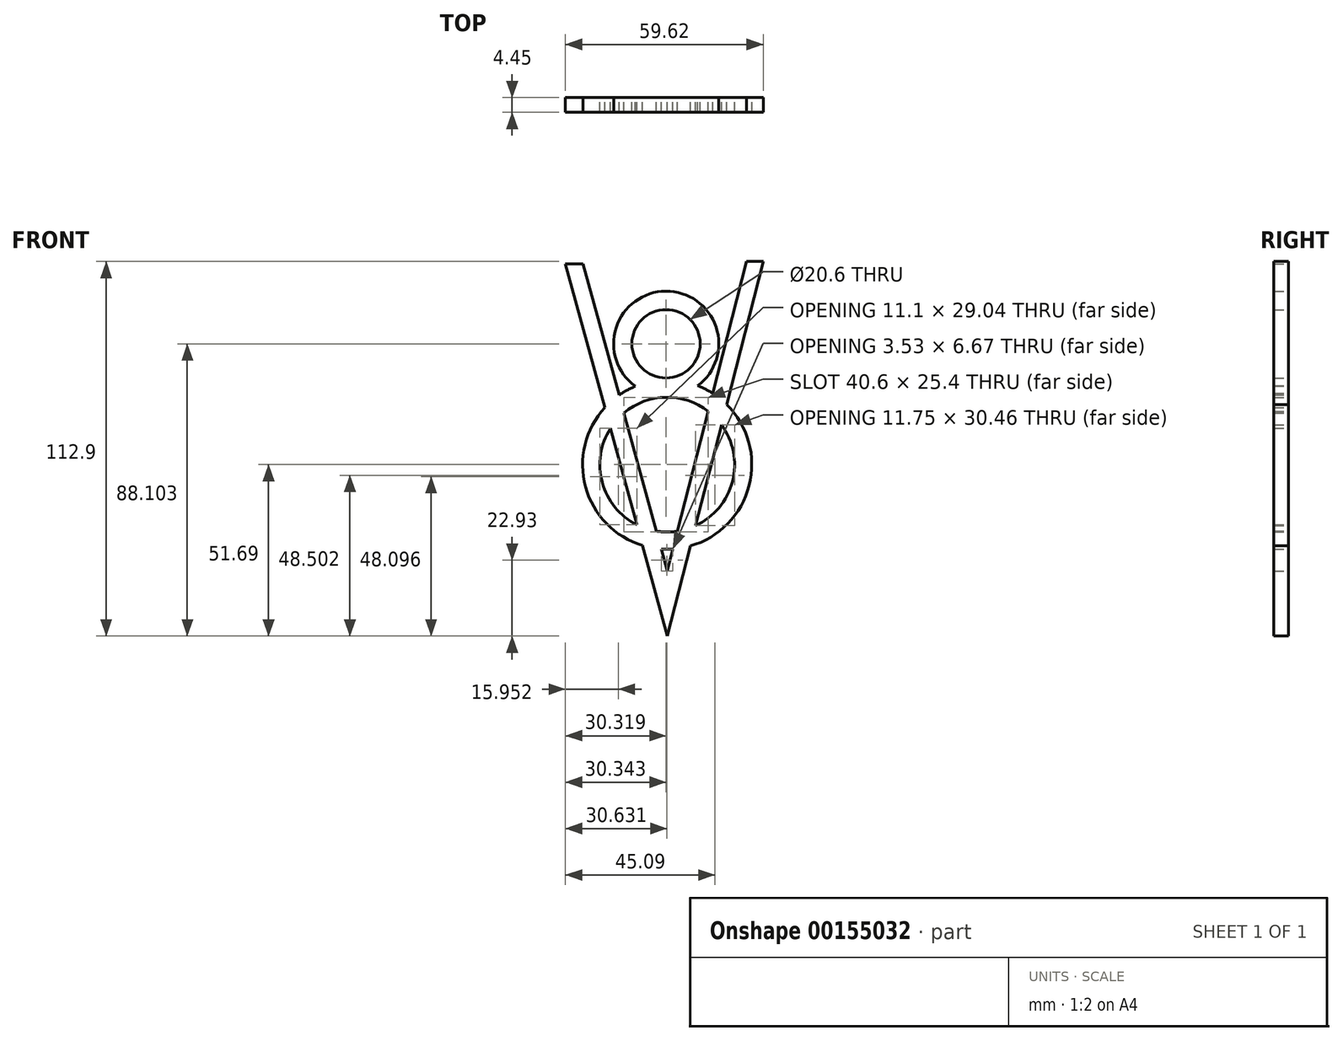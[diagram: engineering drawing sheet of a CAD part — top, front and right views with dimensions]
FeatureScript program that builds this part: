
annotation { "Feature Type Name" : "Feature", "Feature Type Description" : "" }
export const myFeature = defineFeature(function(context is Context, id is Id, definition is map)
    precondition{}
    {
        {
            var Q0;
            Q0=qCreatedBy(makeId("Front.planeOp"),FACE);
            var sketch = newSketch(context, id + "F0", { "sketchPlane" : qUnion([Q0])});
            skLineSegment(sketch, "E0", {"start": v(0, -70.05) * mm, "end": v(-7.47, -42.73) * mm});
            skLineSegment(sketch, "E1", {"start": v(-30.7, 42.12) * mm, "end": v(-25.33, 42.12) * mm});
            skLineSegment(sketch, "E2", {"start": v(-25.33, 42.12) * mm, "end": v(-14.52, 2.6) * mm});
            skLineSegment(sketch, "E3", {"start": v(0, -50.45) * mm, "end": v(1.7, -43.8) * mm});
            skLineSegment(sketch, "E4", {"start": v(23.9, 42.85) * mm, "end": v(28.93, 42.85) * mm});
            skLineSegment(sketch, "E5", {"start": v(28.93, 42.85) * mm, "end": v(17.9, -0.22) * mm});
            skArc(sketch, "E6", {"start": v(-9.6, 5.26) * mm, "mid": v(-12.13, 4.07) * mm, "end": v(-14.52, 2.6) * mm});
            skPoint(sketch, "E6.first.point", {"position": v(-24.9, -12.84) * mm});
            skPoint(sketch, "E6.second.point", {"position": v(13.12, -40.2) * mm});
            skPoint(sketch, "E6.third.point", {"position": v(23.56, -8.67) * mm});
            skPoint(sketch, "E7.first.point", {"position": v(19.2, 21.93) * mm});
            skPoint(sketch, "E7.second.point", {"position": v(-11.63, 34.45) * mm});
            skPoint(sketch, "E7.third.point", {"position": v(-14.88, 4.54) * mm});
            skArc(sketch, "E8", {"start": v(9.18, 5.41) * mm, "mid": v(-0.44, 33.93) * mm, "end": v(-9.6, 5.26) * mm});
            skPoint(sketch, "E8.first.point", {"position": v(-13.59, 26.73) * mm});
            skPoint(sketch, "E8.second.point", {"position": v(14, 24.88) * mm});
            skPoint(sketch, "E8.third.point", {"position": v(11.45, 7.49) * mm});
            skCircle(sketch, "E9", {"center": v(-0.37, 18.05) * mm, "radius": 10.3 * mm});
            skPoint(sketch, "E9.first.point", {"position": v(3.34, 27.66) * mm});
            skPoint(sketch, "E9.second.point", {"position": v(8.2, 12.36) * mm});
            skPoint(sketch, "E9.third.point", {"position": v(-8.26, 11.43) * mm});
            skArc(sketch, "E10", {"start": v(-17.13, -7.43) * mm, "mid": v(-19.6, -23.72) * mm, "end": v(-9.19, -36.48) * mm});
            skPoint(sketch, "E10.first.point", {"position": v(-18.52, -10) * mm});
            skPoint(sketch, "E10.second.point", {"position": v(19.1, -11.55) * mm});
            skPoint(sketch, "E10.third.point", {"position": v(11.95, -34.76) * mm});
            skPoint(sketch, "E10.third.point.positionSnap0", {"position": v(11.95, -3.8) * mm});
            skLineSegment(sketch, "E11.trimOffspring", {"start": v(-13.05, -2.78) * mm, "end": v(-3.3, -38.4) * mm});
            skLineSegment(sketch, "E12.trimOffspring", {"start": v(-18.85, -1.17) * mm, "end": v(-30.7, 42.12) * mm});
            skArc(sketch, "E13.trimOffspring", {"start": v(-18.85, -1.17) * mm, "mid": v(-24.6, -25.09) * mm, "end": v(-7.47, -42.73) * mm});
            skArc(sketch, "E14.trimOffspring", {"start": v(12.35, -2.26) * mm, "mid": v(-0.44, 1.94) * mm, "end": v(-13.05, -2.78) * mm});
            skLineSegment(sketch, "E15.trimOffspring", {"start": v(13.73, 3.1) * mm, "end": v(23.9, 42.85) * mm});
            skLineSegment(sketch, "E16.trimOffspring", {"start": v(16.33, -6.32) * mm, "end": v(8.53, -36.78) * mm});
            skArc(sketch, "E17.trimOffspring", {"start": v(-3.3, -38.4) * mm, "mid": v(-0.1, -38.66) * mm, "end": v(3.08, -38.42) * mm});
            skArc(sketch, "E18.trimOffspring", {"start": v(-1.83, -43.78) * mm, "mid": v(-0.06, -43.85) * mm, "end": v(1.7, -43.8) * mm});
            skLineSegment(sketch, "E19.trimOffspring", {"start": v(-9.19, -36.48) * mm, "end": v(-17.13, -7.43) * mm});
            skLineSegment(sketch, "E20.trimOffspring", {"start": v(-1.83, -43.78) * mm, "end": v(0, -50.45) * mm});
            skLineSegment(sketch, "E21.trimOffspring", {"start": v(3.08, -38.42) * mm, "end": v(12.35, -2.26) * mm});
            skLineSegment(sketch, "E22.trimOffspring", {"start": v(6.96, -42.87) * mm, "end": v(0, -70.05) * mm});
            skArc(sketch, "E23.trimOffspring", {"start": v(8.53, -36.78) * mm, "mid": v(19.65, -23.4) * mm, "end": v(16.33, -6.32) * mm});
            skArc(sketch, "E24.trimOffspring", {"start": v(6.96, -42.87) * mm, "mid": v(25.44, -19.53) * mm, "end": v(9.18, 5.41) * mm});
            skSolve(sketch);
        }
        {
            var Q0;
            Q0 = qSketchRegion(id + "F0", true);
            extrude(context, id + "F1", {"entities" : qUnion([Q0]), "depth" : 4.44 * mm});
        }
    });
